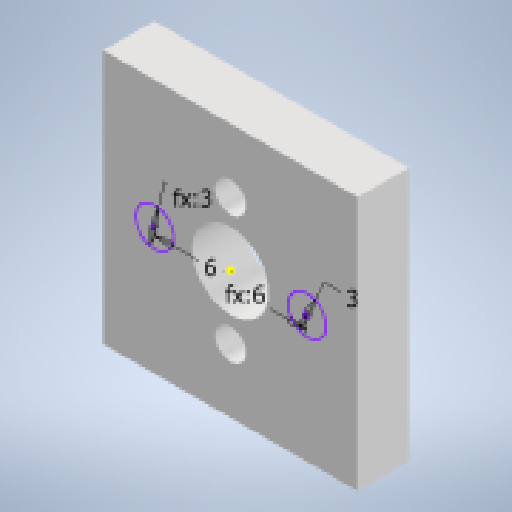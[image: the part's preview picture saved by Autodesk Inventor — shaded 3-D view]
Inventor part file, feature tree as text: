
AUTODESK INVENTOR PART (.ipt)
format: ipt  version: 2023 (Build 270158000, 158)  size: 161,280 bytes
history: native  units: mm
features: extrude x3, sketch x3
ambient origin geometry x8: Origin, YZ Plane, XZ Plane, XY Plane, X Axis, Y Axis, Z Axis, Center Point
bodies: Solid1 (feature_tree)
feature tree (6):
  extrude  "Extrusion1"  Depth=10.0mm
  extrude  "Extrusion2"  Depth=10.0mm
  extrude  "Extrusion3"  Depth=5.0mm
  sketch  "Sketch1"  dims[d0=10.0mm d1=10.0mm]
  sketch  "Sketch2"  dims[d2=10.0mm d3=10.0mm]
  sketch  "Sketch3"  dims[d4=5.0mm d5=5.0mm d6=2.4mm d7=2.4mm d8=6.0mm d9=4.0mm d10=0.0mm d17=40.0mm d18=0.0mm d19=6.0mm d20=10.0mm d21=4.0mm d22=4.0mm d23=4.0mm d24=0.0mm]
